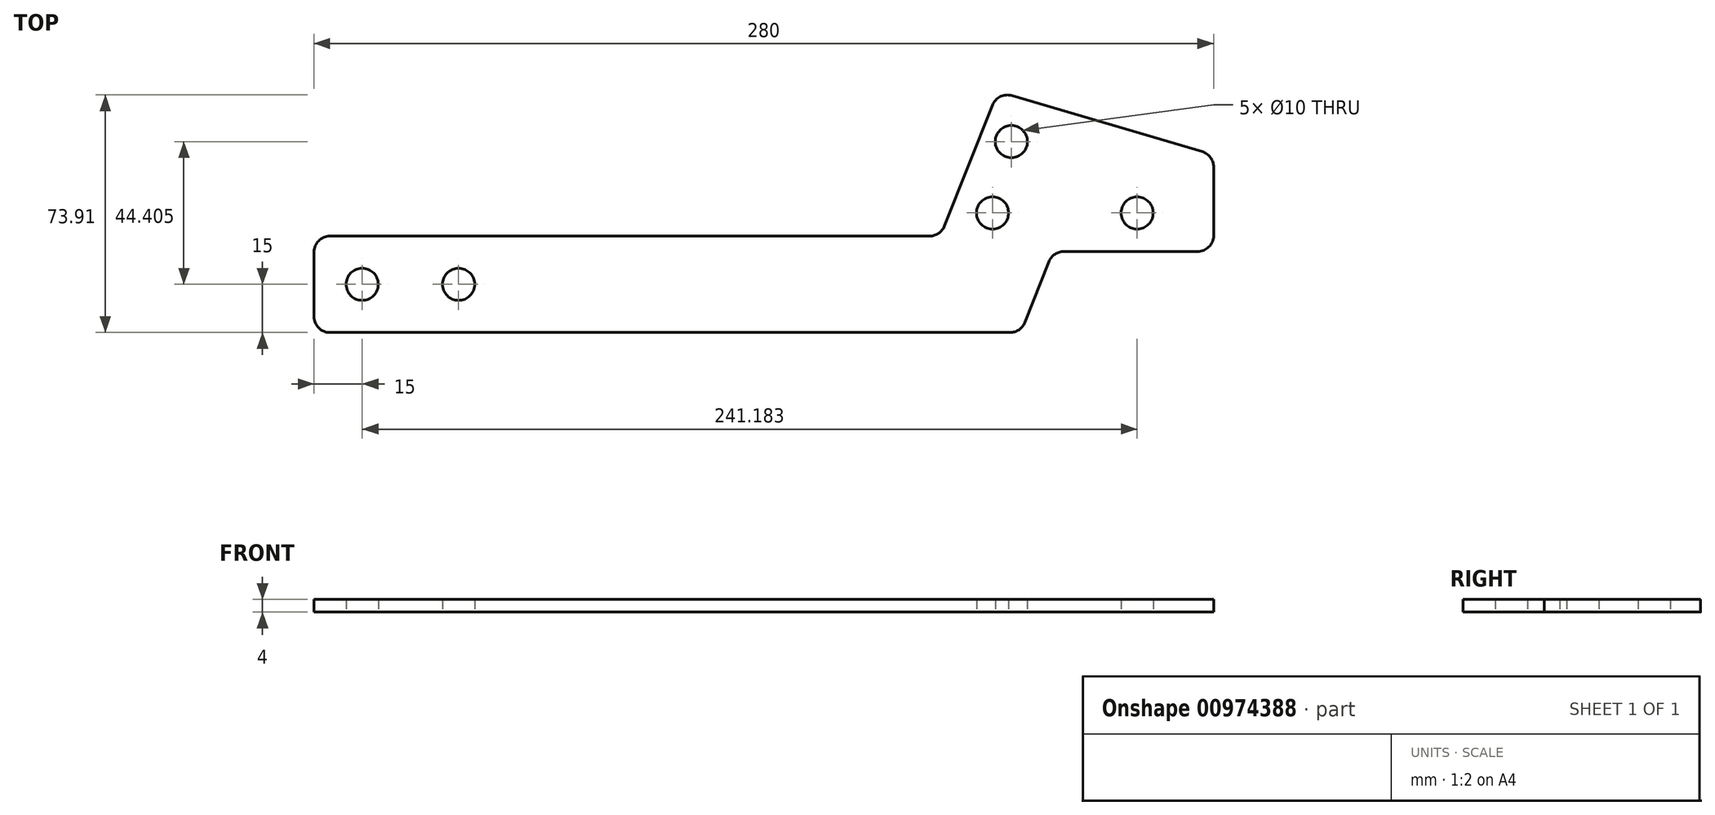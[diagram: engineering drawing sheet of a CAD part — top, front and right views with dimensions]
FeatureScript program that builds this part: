
annotation { "Feature Type Name" : "Feature", "Feature Type Description" : "" }
export const myFeature = defineFeature(function(context is Context, id is Id, definition is map)
    precondition{}
    {
        {
            var Q0;
            Q0=qCreatedBy(makeId("Top.planeOp"),FACE);
            var sketch = newSketch(context, id + "F0", { "sketchPlane" : qUnion([Q0])});
            skLineSegment(sketch, "E0", {"start": v(0, 0) * mm, "end": v(220, 0) * mm});
            skLineSegment(sketch, "E1", {"start": v(220, 0) * mm, "end": v(230, 25.2) * mm});
            skLineSegment(sketch, "E2", {"start": v(230, 25.2) * mm, "end": v(280, 25.2) * mm});
            skLineSegment(sketch, "E3", {"start": v(280, 25.2) * mm, "end": v(280, 55.2) * mm});
            skLineSegment(sketch, "E4", {"start": v(280, 55.2) * mm, "end": v(212.86, 75) * mm});
            skLineSegment(sketch, "E5", {"start": v(212.86, 75) * mm, "end": v(195, 30) * mm});
            skLineSegment(sketch, "E6", {"start": v(195, 30) * mm, "end": v(0, 30) * mm});
            skLineSegment(sketch, "E7", {"start": v(0, 30) * mm, "end": v(0, 0) * mm});
            skLineSegment(sketch, "E8", {"start": v(0, 15) * mm, "end": v(213.95, 15) * mm, "construction": true});
            skCircle(sketch, "E9", {"center": v(15, 15) * mm, "radius": 5 * mm});
            skCircle(sketch, "E10", {"center": v(45, 15) * mm, "radius": 5 * mm});
            skLineSegment(sketch, "E11", {"start": v(270.14, 37.2) * mm, "end": v(200.25, 37.2) * mm, "construction": true});
            skCircle(sketch, "E12", {"center": v(211.18, 37.2) * mm, "radius": 5 * mm});
            skCircle(sketch, "E13", {"center": v(217.04, 59.4) * mm, "radius": 5 * mm});
            skCircle(sketch, "E14", {"center": v(256.18, 37.2) * mm, "radius": 5 * mm});
            skCircle(sketch, "E15", {"center": v(256.18, 37.2) * mm, "radius": 45 * mm, "construction": true});
            skSolve(sketch);
        }
        {
            var Q0;
            Q0 = qSketchRegion(id + "F0", true);
            extrude(context, id + "F1", {"entities" : qUnion([Q0]), "depth" : 4 * mm, "offsetDistance" : 25 * mm});
        }
        {
            var Q0;
            Q0=makeQuery(id+"F1.opExtrude","SWEPT_EDGE",EDGE,{"disambiguationData":[OSD([sQuery(id+"F0.wireOp",EDGE,"E6"),sQuery(id+"F0.wireOp",EDGE,"E7")])]});
            var Q1;
            Q1=makeQuery(id+"F1.opExtrude","SWEPT_EDGE",EDGE,{"disambiguationData":[OSD([sQuery(id+"F0.wireOp",EDGE,"E0"),sQuery(id+"F0.wireOp",EDGE,"E7")])]});
            var Q2;
            Q2=makeQuery(id+"F1.opExtrude","SWEPT_EDGE",EDGE,{"disambiguationData":[OSD([sQuery(id+"F0.wireOp",EDGE,"E0"),sQuery(id+"F0.wireOp",EDGE,"E1")])]});
            var Q3;
            Q3=makeQuery(id+"F1.opExtrude","SWEPT_EDGE",EDGE,{"disambiguationData":[OSD([sQuery(id+"F0.wireOp",EDGE,"E2"),sQuery(id+"F0.wireOp",EDGE,"E3")])]});
            var Q4;
            Q4=makeQuery(id+"F1.opExtrude","SWEPT_EDGE",EDGE,{"disambiguationData":[OSD([sQuery(id+"F0.wireOp",EDGE,"E3"),sQuery(id+"F0.wireOp",EDGE,"E4")])]});
            var Q5;
            Q5=makeQuery(id+"F1.opExtrude","SWEPT_EDGE",EDGE,{"disambiguationData":[OSD([sQuery(id+"F0.wireOp",EDGE,"E4"),sQuery(id+"F0.wireOp",EDGE,"E5")])]});
            var Q6;
            Q6=makeQuery(id+"F1.opExtrude","SWEPT_EDGE",EDGE,{"disambiguationData":[OSD([sQuery(id+"F0.wireOp",EDGE,"E5"),sQuery(id+"F0.wireOp",EDGE,"E6")])]});
            var Q7;
            Q7=makeQuery(id+"F1.opExtrude","SWEPT_EDGE",EDGE,{"disambiguationData":[OSD([sQuery(id+"F0.wireOp",EDGE,"E1"),sQuery(id+"F0.wireOp",EDGE,"E2")])]});
            fillet(context, id + "F2", {"entities" : qUnion([Q0, Q1, Q2, Q3, Q4, Q5, Q6, Q7]), "radius" : 5 * mm, "tangentPropagation" : true, "allowEdgeOverflow" : false});
        }
    });
